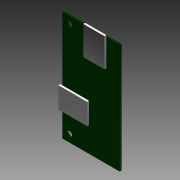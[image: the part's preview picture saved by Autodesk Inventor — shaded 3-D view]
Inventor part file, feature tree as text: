
AUTODESK INVENTOR PART (.ipt)
format: ipt  version: 2013 (Build 170138000, 138)  size: 133,632 bytes
history: native  units: in
note: dims shown in document units (in); Inventor stores cm internally (conversion verified against a paired STEP export)
features: extrude x2, sketch x2
ambient origin geometry x8: Origin, YZ Plane, XZ Plane, XY Plane, X Axis, Y Axis, Z Axis, Center Point
bodies: Solid1 (feature_tree)
feature tree (4):
  extrude  "Extrusion1"  Depth=1.1811in
  extrude  "Extrusion4"  Depth=0.1102in
  sketch  "Sketch1"  dims[d0=0.0394in d1=0.0in d2=1.1811in]
  sketch  "Sketch4"  dims[d4=2.25in d6=0.1102in d21=0.15in d22=0.15in d23=0.15in d24=0.15in d25=0.5906in d26=0.4331in d27=0.0394in d28=0.0394in d29=0.0in d30=0.5118in d31=0.4331in d32=0.5906in d33=0.0394in d35=0.4724in]
